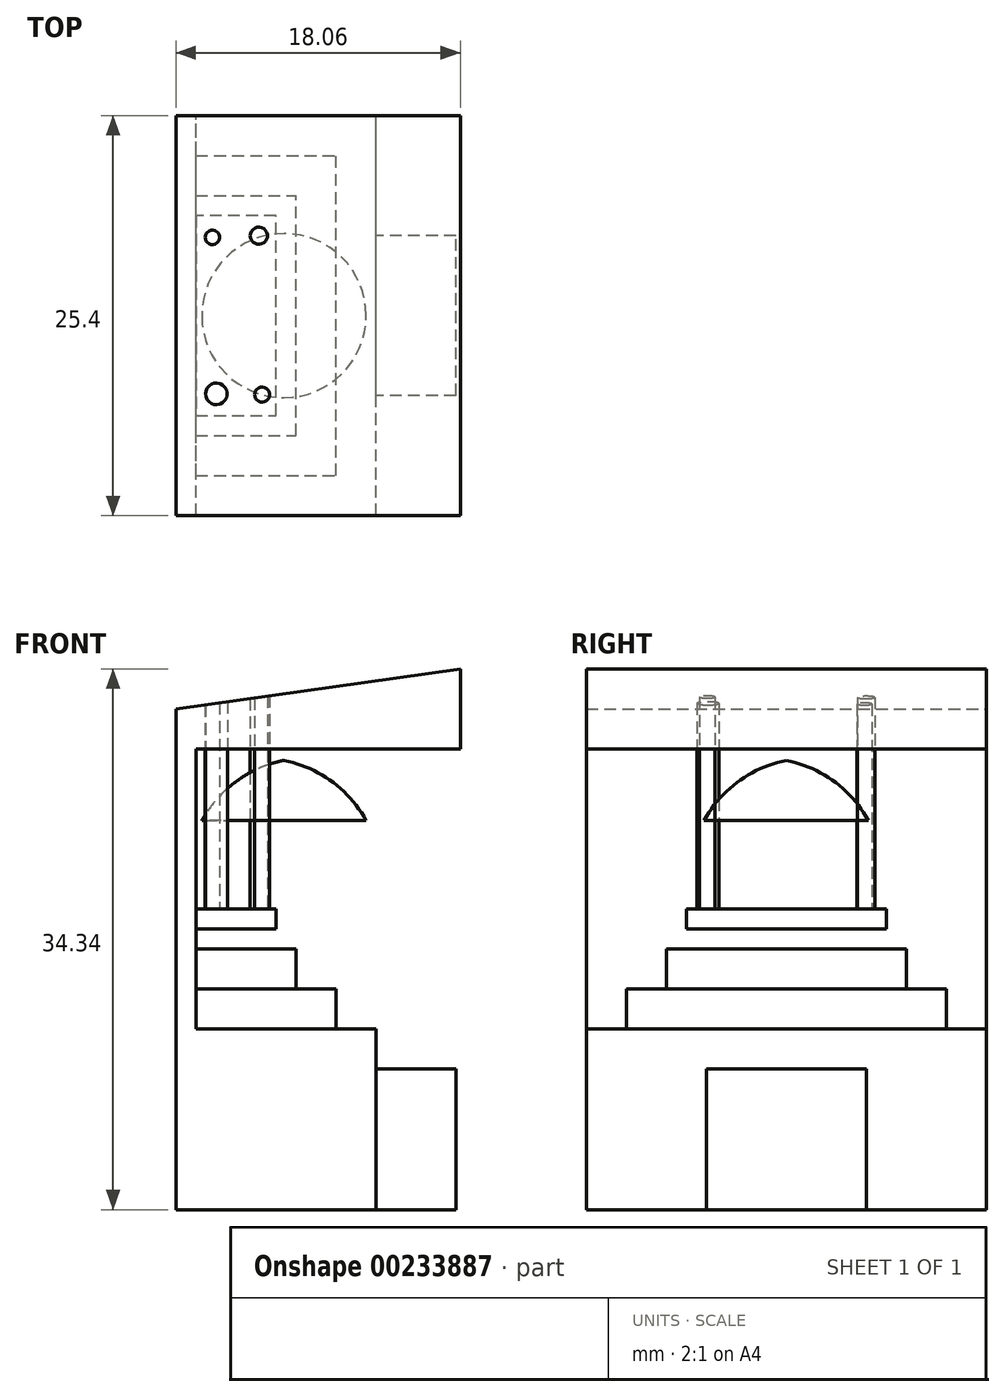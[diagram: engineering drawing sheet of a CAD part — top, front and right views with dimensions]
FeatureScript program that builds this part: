
annotation { "Feature Type Name" : "Feature", "Feature Type Description" : "" }
export const myFeature = defineFeature(function(context is Context, id is Id, definition is map)
    precondition{}
    {
        {
            var Q0;
            Q0=qCreatedBy(makeId("Front.planeOp"),FACE);
            var sketch = newSketch(context, id + "F0", { "sketchPlane" : qUnion([Q0])});
            skLineSegment(sketch, "E0", {"start": v(0, 0) * mm, "end": v(12.7, 0) * mm});
            skLineSegment(sketch, "E1", {"start": v(12.7, 0) * mm, "end": v(12.7, 11.48) * mm});
            skLineSegment(sketch, "E2", {"start": v(12.7, 11.48) * mm, "end": v(1.27, 11.48) * mm});
            skLineSegment(sketch, "E3", {"start": v(1.27, 11.48) * mm, "end": v(1.27, 29.26) * mm});
            skLineSegment(sketch, "E4", {"start": v(0, 31.8) * mm, "end": v(0, 0) * mm});
            skLineSegment(sketch, "E5", {"start": v(12.7, 8.94) * mm, "end": v(17.78, 8.94) * mm});
            skLineSegment(sketch, "E6", {"start": v(17.78, 8.94) * mm, "end": v(17.78, 0) * mm});
            skLineSegment(sketch, "E7", {"start": v(17.78, 0) * mm, "end": v(12.7, 0) * mm});
            skLineSegment(sketch, "E8", {"start": v(1.27, 14.02) * mm, "end": v(10.16, 14.02) * mm});
            skLineSegment(sketch, "E9", {"start": v(10.16, 14.02) * mm, "end": v(10.16, 11.48) * mm});
            skLineSegment(sketch, "E10", {"start": v(1.27, 16.56) * mm, "end": v(7.62, 16.56) * mm});
            skLineSegment(sketch, "E11", {"start": v(7.62, 16.56) * mm, "end": v(7.62, 14.02) * mm});
            skLineSegment(sketch, "E12", {"start": v(1.27, 29.26) * mm, "end": v(18.06, 29.26) * mm});
            skLineSegment(sketch, "E13", {"start": v(18.06, 29.26) * mm, "end": v(18.06, 34.34) * mm});
            skLineSegment(sketch, "E14", {"start": v(18.06, 34.34) * mm, "end": v(0, 31.8) * mm});
            skSolve(sketch);
        }
        {
            var Q0;
            {var subQ3=sQuery(id+"F0.wireOp",EDGE,"E0");Q0=makeQuery(id+"F0.imprint","IMPRINT",FACE,{"disambiguationData":[TD([[makeQuery(id+"F0.imprint","IMPRINT",EDGE,{"derivedFrom":subQ3}),1.0]])]});}
            extrude(context, id + "F1", {"entities" : qUnion([Q0]), "endBound" : BoundingType.SYMMETRIC, "depth" : 25.4 * mm});
        }
        {
            var Q0;
            {var subQ2=sQuery(id+"F0.wireOp",EDGE,"E5");Q0=makeQuery(id+"F0.imprint","IMPRINT",FACE,{"disambiguationData":[TD([[makeQuery(id+"F0.imprint","IMPRINT",EDGE,{"derivedFrom":subQ2}),-1.0]])]});}
            extrude(context, id + "F2", {"entities" : qUnion([Q0]), "operationType" : NewBodyOperationType.ADD, "endBound" : BoundingType.SYMMETRIC, "depth" : 10.16 * mm});
        }
        {
            var Q0;
            {var subQ0=sQuery(id+"F0.wireOp",EDGE,"E9");Q0=makeQuery(id+"F0.imprint","IMPRINT",FACE,{"disambiguationData":[TD([[makeQuery(id+"F0.imprint","IMPRINT",EDGE,{"derivedFrom":subQ0}),-1.0]])]});}
            extrude(context, id + "F3", {"entities" : qUnion([Q0]), "operationType" : NewBodyOperationType.ADD, "endBound" : BoundingType.SYMMETRIC, "depth" : 20.32 * mm});
        }
        {
            var Q0;
            {var subQ3=sQuery(id+"F0.wireOp",EDGE,"E10");Q0=makeQuery(id+"F0.imprint","IMPRINT",FACE,{"disambiguationData":[TD([[makeQuery(id+"F0.imprint","IMPRINT",EDGE,{"derivedFrom":subQ3}),-1.0]])]});}
            extrude(context, id + "F4", {"entities" : qUnion([Q0]), "operationType" : NewBodyOperationType.ADD, "endBound" : BoundingType.SYMMETRIC, "depth" : 15.24 * mm});
        }
        {
            var Q0;
            Q0=qCreatedBy(makeId("Front.planeOp"),FACE);
            var sketch = newSketch(context, id + "F5", { "sketchPlane" : qUnion([Q0])});
            skLineSegment(sketch, "E15", {"start": v(6.86, 35.92) * mm, "end": v(6.86, 21.73) * mm, "construction": true});
            skLineSegment(sketch, "E16", {"start": v(1.64, 24.73) * mm, "end": v(6.86, 24.73) * mm});
            skArc(sketch, "E17", {"start": v(6.86, 28.54) * mm, "mid": v(3.83, 27.2) * mm, "end": v(1.64, 24.73) * mm});
            skLineSegment(sketch, "E18", {"start": v(6.86, 24.73) * mm, "end": v(6.86, 28.54) * mm});
            skSolve(sketch);
        }
        {
            var Q0;
            Q0=makeQuery(id+"F5.imprint","IMPRINT",FACE,{"disambiguationData":[TD([[makeQuery(id+"F5.imprint","IMPRINT",EDGE,{"derivedFrom":sQuery(id+"F5.wireOp",EDGE,"E16")}),1.0]])]});
            var Q1;
            Q1=sQuery(id+"F5.wireOp",EDGE,"E15");
            revolve(context, id + "F6", {"operationType" : NewBodyOperationType.ADD, "entities" : qUnion([Q0]), "axis" : qUnion([Q1]), "revolveType" : RevolveType.FULL});
        }
        {
            var Q0;
            Q0=makeQuery(id+"F4.opExtrude","SWEPT_FACE",FACE,{"disambiguationData":[OSD([sQuery(id+"F0.wireOp",EDGE,"E10")])]});
            cPlane(context, id + "F7", {"entities" : qUnion([Q0]), "cplaneType" : CPlaneType.OFFSET, "offset" : 1.27 * mm, "width" : 152.4 * mm, "height" : 152.4 * mm});
        }
        {
            var Q0;
            Q0=qCreatedBy(id+"F7.planeOp",FACE);
            var sketch = newSketch(context, id + "F8", { "sketchPlane" : qUnion([Q0])});
            skLineSegment(sketch, "E19.0.0", {"start": v(18.06, 12.7) * mm, "end": v(0, 12.7) * mm});
            skLineSegment(sketch, "E19.0.1", {"start": v(0, 12.7) * mm, "end": v(0, -12.7) * mm});
            skLineSegment(sketch, "E19.0.2", {"start": v(0, -12.7) * mm, "end": v(18.06, -12.7) * mm});
            skLineSegment(sketch, "E19.0.3", {"start": v(18.06, -12.7) * mm, "end": v(18.06, 12.7) * mm});
            skLineSegment(sketch, "E20", {"start": v(0, 0) * mm, "end": v(0, -6.35) * mm});
            skLineSegment(sketch, "E21", {"start": v(0, -6.35) * mm, "end": v(6.35, -6.35) * mm});
            skLineSegment(sketch, "E22", {"start": v(6.35, -6.35) * mm, "end": v(6.35, 6.35) * mm});
            skLineSegment(sketch, "E23", {"start": v(6.35, 6.35) * mm, "end": v(0, 6.35) * mm});
            skLineSegment(sketch, "E24.0.0", {"start": v(7.62, 7.62) * mm, "end": v(1.27, 7.62) * mm});
            skLineSegment(sketch, "E24.0.1", {"start": v(1.27, 7.62) * mm, "end": v(1.27, -7.62) * mm});
            skLineSegment(sketch, "E24.0.2", {"start": v(1.27, -7.62) * mm, "end": v(7.62, -7.62) * mm});
            skLineSegment(sketch, "E24.0.3", {"start": v(7.62, -7.62) * mm, "end": v(7.62, 7.62) * mm});
            skSolve(sketch);
        }
        {
            var Q0;
            {var subQ0=sQuery(id+"F8.wireOp",EDGE,"E22");Q0=makeQuery(id+"F8.imprint","IMPRINT",FACE,{"disambiguationData":[TD([[makeQuery(id+"F8.imprint","IMPRINT",EDGE,{"derivedFrom":subQ0}),1.0]])]});}
            extrude(context, id + "F9", {"entities" : qUnion([Q0]), "operationType" : NewBodyOperationType.ADD, "depth" : 1.27 * mm});
        }
        {
            var Q0;
            Q0=makeQuery(id+"F9.opExtrude","CAP_FACE",FACE,{"disambiguationData":[OSD([sQuery(id+"F8.wireOp",EDGE,"E21"),sQuery(id+"F8.wireOp",EDGE,"E22"),sQuery(id+"F8.wireOp",EDGE,"E23"),sQuery(id+"F8.wireOp",EDGE,"E24.0.1")])],"isStart":false});
            var sketch = newSketch(context, id + "F10", { "sketchPlane" : qUnion([Q0])});
            skCircle(sketch, "E25", {"center": v(2.56, -4.97) * mm, "radius": 0.7 * mm});
            skCircle(sketch, "E26", {"center": v(5.46, -5.02) * mm, "radius": 0.48 * mm});
            skCircle(sketch, "E27", {"center": v(2.32, 4.97) * mm, "radius": 0.47 * mm});
            skCircle(sketch, "E28", {"center": v(5.27, 5.07) * mm, "radius": 0.55 * mm});
            skPoint(sketch, "E29.0.2.start.orphan", {"position": v(0, -12.7) * mm});
            skPoint(sketch, "E29.0.3.start.orphan", {"position": v(18.06, -12.7) * mm});
            skPoint(sketch, "E29.0.0.end.orphan", {"position": v(0, 12.7) * mm});
            skPoint(sketch, "E29.0.0.start.orphan", {"position": v(18.06, 12.7) * mm});
            skPoint(sketch, "E30.0.0.end.orphan", {"position": v(1.27, 6.35) * mm});
            skPoint(sketch, "E30.0.3.end.orphan", {"position": v(6.35, 6.35) * mm});
            skPoint(sketch, "E30.0.2.end.orphan", {"position": v(6.35, -6.35) * mm});
            skPoint(sketch, "E30.0.2.start.orphan", {"position": v(1.27, -6.35) * mm});
            skSolve(sketch);
        }
        {
            var Q0;
            Q0 = qSketchRegion(id + "F10", true);
            var Q1;
            Q1=makeQuery(id+"F1.opExtrude","SWEPT_FACE",FACE,{"disambiguationData":[OSD([sQuery(id+"F0.wireOp",EDGE,"E14")])]});
            extrude(context, id + "F11", {"entities" : qUnion([Q0]), "endBound" : BoundingType.UP_TO_SURFACE, "endBoundEntityFace" : qUnion([Q1]), "depth" : 25.4 * mm});
        }
    });
